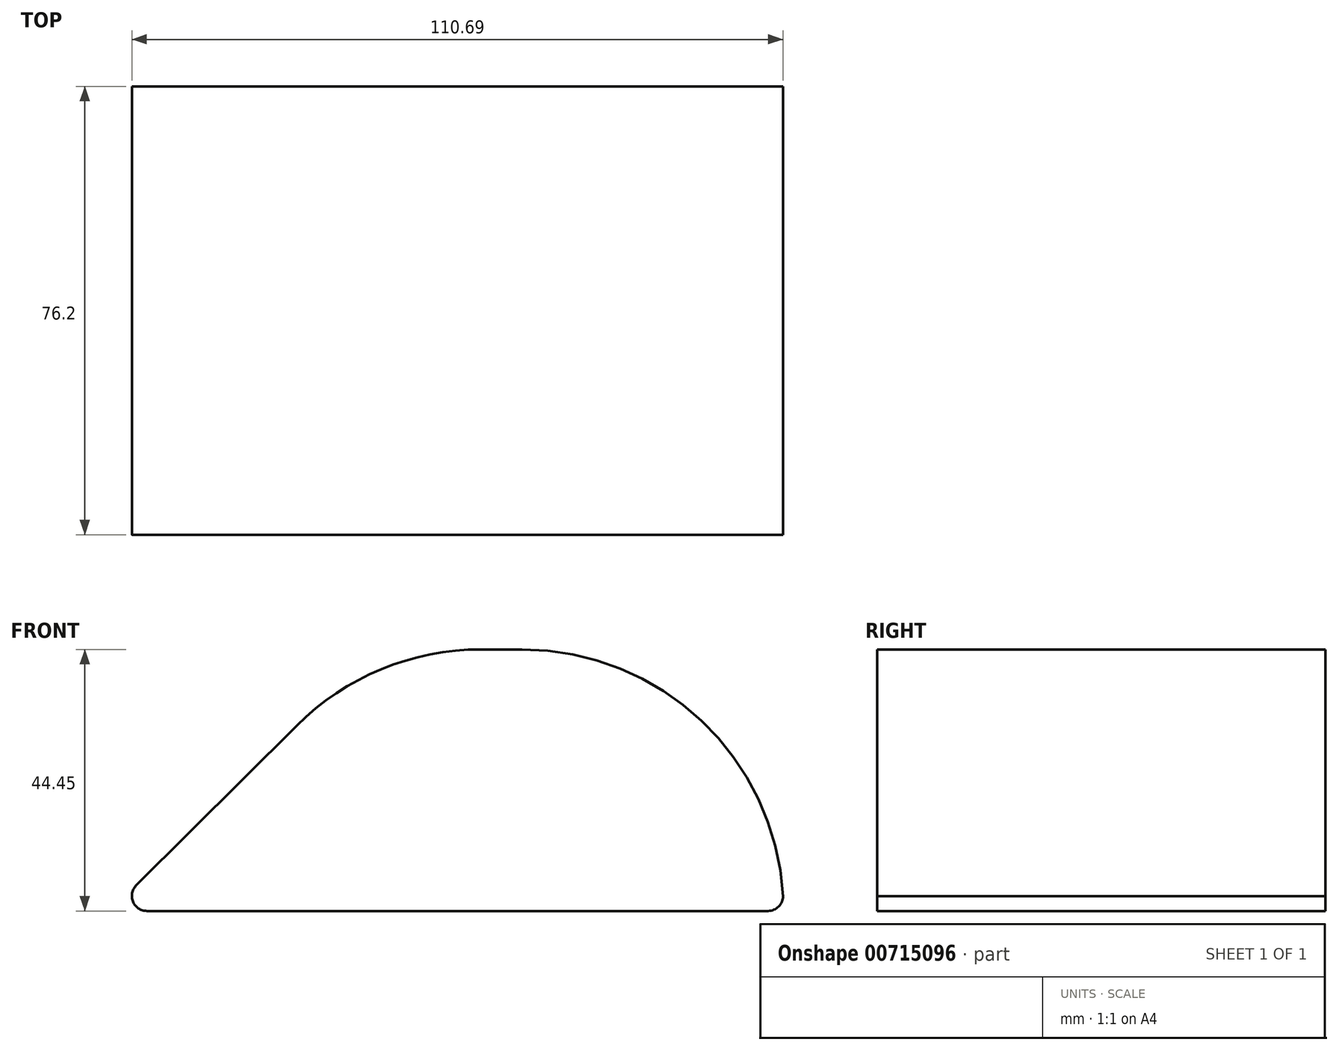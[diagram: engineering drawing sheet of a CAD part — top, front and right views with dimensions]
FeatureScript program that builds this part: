
annotation { "Feature Type Name" : "Feature", "Feature Type Description" : "" }
export const myFeature = defineFeature(function(context is Context, id is Id, definition is map)
    precondition{}
    {
        {
            var Q0;
            Q0=qCreatedBy(makeId("Front.planeOp"),FACE);
            var sketch = newSketch(context, id + "F0", { "sketchPlane" : qUnion([Q0])});
            skLineSegment(sketch, "E0.bottom", {"start": v(0, 0) * mm, "end": v(114.3, 0) * mm});
            skLineSegment(sketch, "E0.top", {"start": v(0, 44.45) * mm, "end": v(114.3, 44.45) * mm});
            skLineSegment(sketch, "E0.left", {"start": v(0, 0) * mm, "end": v(0, 44.45) * mm});
            skLineSegment(sketch, "E0.right", {"start": v(114.3, 0) * mm, "end": v(114.3, 44.45) * mm});
            skLineSegment(sketch, "E1", {"start": v(114.3, 22.23) * mm, "end": v(0, 22.23) * mm, "construction": true});
            skLineSegment(sketch, "E2", {"start": v(0, 0) * mm, "end": v(44.62, 44.45) * mm});
            skSolve(sketch);
        }
        {
            var Q0;
            Q0=makeQuery(id+"F0.imprint","IMPRINT",FACE,{"disambiguationData":[TD([[makeQuery(id+"F0.imprint","IMPRINT",EDGE,{"derivedFrom":sQuery(id+"F0.wireOp",EDGE,"E0.bottom")}),1.0]])]});
            extrude(context, id + "F1", {"entities" : qUnion([Q0]), "depth" : 76.2 * mm, "offsetDistance" : 25.4 * mm});
        }
        {
            var Q0;
            Q0=makeQuery(id+"F1.opExtrude","SWEPT_EDGE",EDGE,{"disambiguationData":[OSD([sQuery(id+"F0.wireOp",EDGE,"E0.bottom"),sQuery(id+"F0.wireOp",EDGE,"E0.left"),sQuery(id+"F0.wireOp",EDGE,"u8WCmLtB-BU6p-FgaY-QpDy-i7tAeueijXhj")])]});
            var Q1;
            Q1=makeQuery(id+"F1.opExtrude","SWEPT_EDGE",EDGE,{"disambiguationData":[OSD([sQuery(id+"F0.wireOp",EDGE,"E0.bottom"),sQuery(id+"F0.wireOp",EDGE,"E0.right")])]});
            fillet(context, id + "F2", {"entities" : qUnion([Q0, Q1]), "radius" : 2.54 * mm, "tangentPropagation" : true, "allowEdgeOverflow" : false});
        }
        {
            var Q0;
            Q0=makeQuery(id+"F1.opExtrude","SWEPT_EDGE",EDGE,{"disambiguationData":[OSD([sQuery(id+"F0.wireOp",EDGE,"E0.top"),sQuery(id+"F0.wireOp",EDGE,"u8WCmLtB-BU6p-FgaY-QpDy-i7tAeueijXhj")])]});
            fillet(context, id + "F3", {"entities" : qUnion([Q0]), "radius" : 44.45 * mm, "tangentPropagation" : true, "allowEdgeOverflow" : false});
        }
    });
